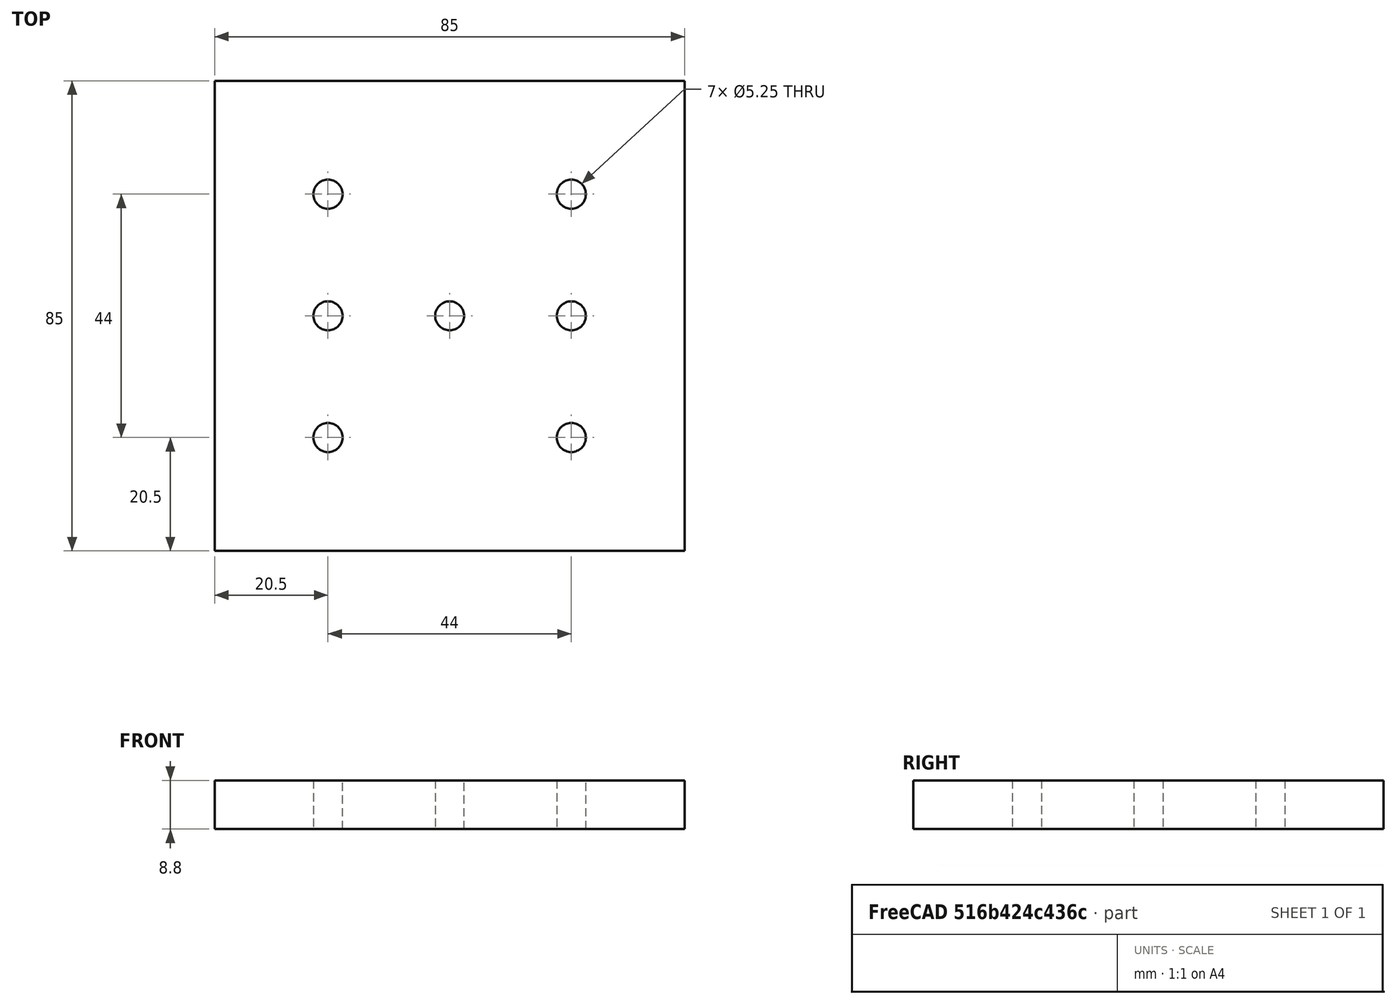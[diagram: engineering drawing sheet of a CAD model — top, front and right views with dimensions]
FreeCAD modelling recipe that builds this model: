
FCSTD DOCUMENT  (FreeCAD 0.21R33771 (Git))
Label: diffuser
License: All rights reserved
LicenseURL: https://en.wikipedia.org/wiki/All_rights_reserved
objects: Sketcher::SketchObject×1, PartDesign::Pad×1, PartDesign::Body×1
note: 4 computed .brp shape members not serialized (recipe doc carries the construction recipe); baked Part::Feature solids carry a one-line shape summary decoded from their .brp

FEATURE [Sketcher::SketchObject] Sketch  label="Base Plate Sketch"
  FullyConstrained = true
  MapMode = 5
  Support = -> [XY_Plane]
  sketch-geometry (23):
    g0: Circle CenterX=-22 CenterY=22 CenterZ=0 NormalX=0 NormalY=0 NormalZ=1 AngleXU=0 Radius=2.625
    g1: Circle CenterX=-22 CenterY=0 CenterZ=0 NormalX=0 NormalY=0 NormalZ=1 AngleXU=0 Radius=2.625
    g2: Circle CenterX=-22 CenterY=-22 CenterZ=0 NormalX=0 NormalY=0 NormalZ=1 AngleXU=0 Radius=2.625
    g3: Circle CenterX=0 CenterY=0 CenterZ=0 NormalX=0 NormalY=0 NormalZ=1 AngleXU=0 Radius=2.625
    g4: Circle CenterX=22 CenterY=22 CenterZ=0 NormalX=0 NormalY=0 NormalZ=1 AngleXU=0 Radius=2.625
    g5: Circle CenterX=22 CenterY=0 CenterZ=0 NormalX=0 NormalY=0 NormalZ=1 AngleXU=0 Radius=2.625
    g6: Circle CenterX=22 CenterY=-22 CenterZ=0 NormalX=0 NormalY=0 NormalZ=1 AngleXU=0 Radius=2.625
    g7: LineSegment StartX=-22 StartY=0 StartZ=0 EndX=-22 EndY=22 EndZ=0
    g8: LineSegment StartX=-22 StartY=0 StartZ=0 EndX=-22 EndY=-22 EndZ=0
    g9: LineSegment StartX=-22 StartY=0 StartZ=0 EndX=0 EndY=0 EndZ=0
    g10: LineSegment StartX=22 StartY=0 StartZ=0 EndX=22 EndY=22 EndZ=0
    g11: LineSegment StartX=22 StartY=0 StartZ=0 EndX=22 EndY=-22 EndZ=0
    g12: LineSegment StartX=22 StartY=0 StartZ=0 EndX=0 EndY=0 EndZ=0
    g13: LineSegment StartX=-42.5 StartY=-42.5 StartZ=0 EndX=-42.5 EndY=42.5 EndZ=0
    g14: LineSegment StartX=-42.5 StartY=42.5 StartZ=0 EndX=42.5 EndY=42.5 EndZ=0
    g15: LineSegment StartX=42.5 StartY=42.5 StartZ=0 EndX=42.5 EndY=-42.5 EndZ=0
    g16: LineSegment StartX=42.5 StartY=-42.5 StartZ=0 EndX=-42.5 EndY=-42.5 EndZ=0
    g17: GeomPoint X=0 Y=0 Z=0
    g18: LineSegment StartX=-40.5 StartY=-40.5 StartZ=0 EndX=-40.5 EndY=40.5 EndZ=0
    g19: LineSegment StartX=-40.5 StartY=40.5 StartZ=0 EndX=40.5 EndY=40.5 EndZ=0
    g20: LineSegment StartX=40.5 StartY=40.5 StartZ=0 EndX=40.5 EndY=-40.5 EndZ=0
    g21: LineSegment StartX=40.5 StartY=-40.5 StartZ=0 EndX=-40.5 EndY=-40.5 EndZ=0
    g22: GeomPoint X=0 Y=0 Z=0
  constraints (56):
    c: Coincident(g3,g-1)
    c: PointOnObject(g5,g-1)
    c: PointOnObject(g1,g-1)
    c: Equal(g4,g5)
    c: Equal(g6,g5)
    c: Equal(g1,g3)
    c: Equal(g0,g1)
    c: Equal(g1,g2)
    c: Equal(g3,g6)
    c: Diameter(g6) = 5.25
    c: Coincident(g7,g1)
    c: Coincident(g7,g0)
    c: Vertical(g7)
    c: Coincident(g8,g1)
    c: Coincident(g8,g2)
    c: Vertical(g8)
    c: Coincident(g9,g1)
    c: Coincident(g9,g3)
    c: Coincident(g10,g5)
    c: Coincident(g10,g4)
    c: Coincident(g11,g5)
    c: Coincident(g11,g6)
    c: Coincident(g12,g5)
    c: Coincident(g12,g3)
    c: Vertical(g11)
    c: Vertical(g10)
    c: Equal(g10,g11)
    c: Equal(g11,g12)
    c: Equal(g9,g12)
    c: Equal(g7,g10)
    c: Equal(g11,g8)
    c: Coincident(g13,g14)
    c: Coincident(g14,g15)
    c: Coincident(g15,g16)
    c: Coincident(g16,g13)
    c: Horizontal(g14)
    c: Horizontal(g16)
    c: Vertical(g13)
    c: Vertical(g15)
    c: Symmetric(g14,g13,g17)
    c: Coincident(g17,g3)
    c: Equal(g14,g15)
    c: DistanceX(g14,g14) = 85
    c: Coincident(g18,g19)
    c: Coincident(g19,g20)
    c: Coincident(g20,g21)
    c: Coincident(g21,g18)
    c: Horizontal(g19)
    c: Horizontal(g21)
    c: Vertical(g18)
    c: Vertical(g20)
    c: Symmetric(g19,g18,g22)
    c: Coincident(g22,g3)
    c: DistanceY(g19,g14) = 2
    c: Equal(g19,g20)
    c: DistanceX(g12,g12) = 22
FEATURE [PartDesign::Pad] Pad  label="Base Plate Pad"
  Direction = (0,0,1)
  Length = 8.8
  Length2 = 10
  Profile = -> Sketch
  ReferenceAxis = -> Sketch [N_Axis]
  Type = 0
FEATURE [PartDesign::Body] Body  label="Solid"
  Group = -> [Sketch,Pad]
  Origin = -> Origin
  Tip = -> Pad
